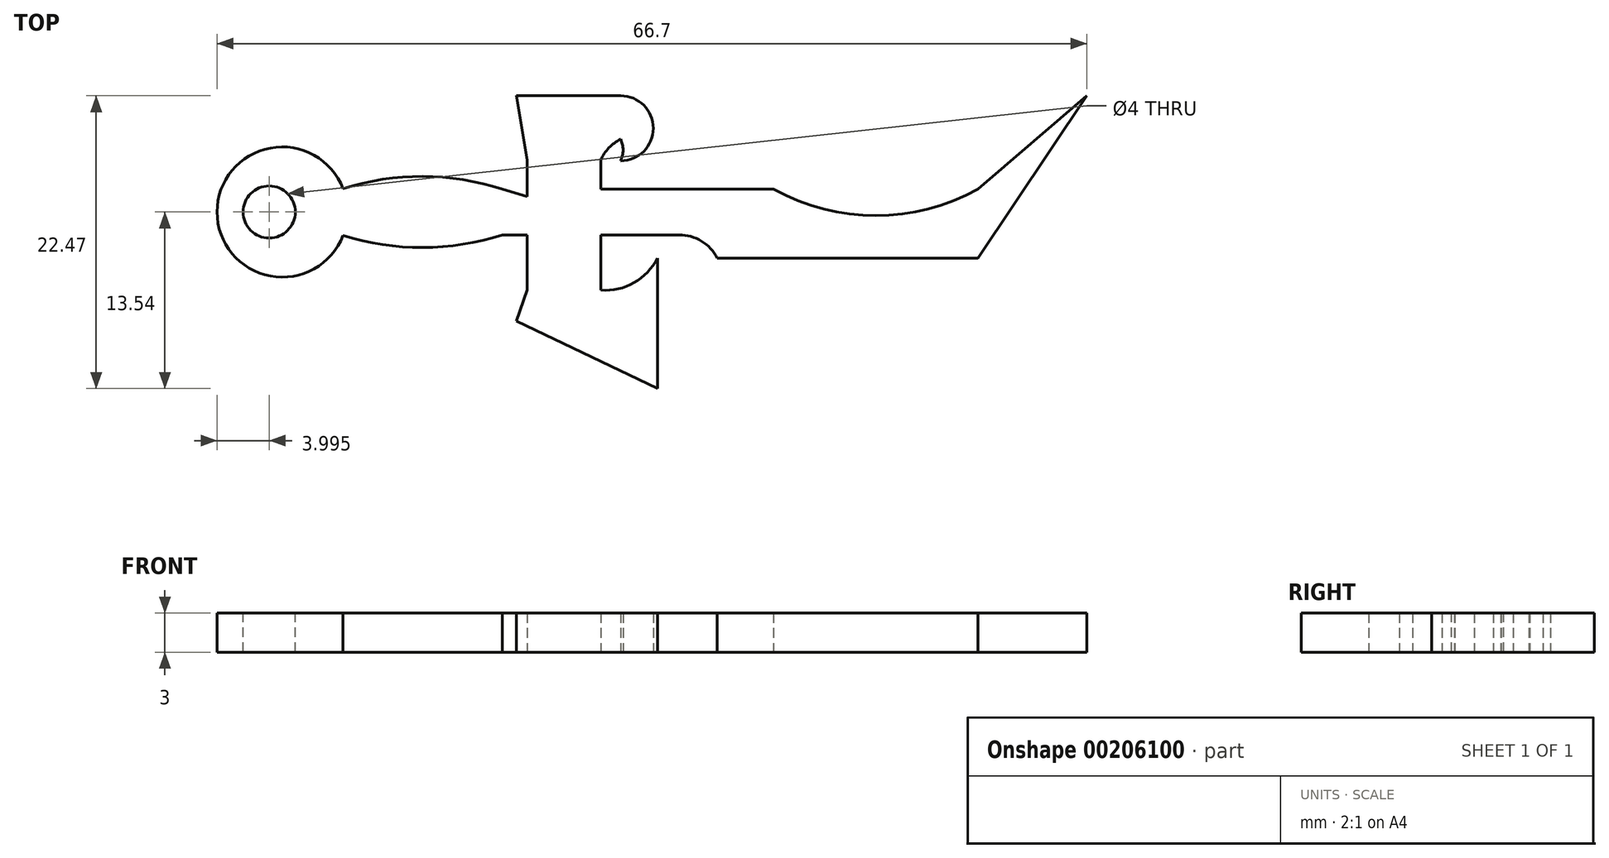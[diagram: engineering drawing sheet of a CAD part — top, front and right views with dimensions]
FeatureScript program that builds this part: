
annotation { "Feature Type Name" : "Feature", "Feature Type Description" : "" }
export const myFeature = defineFeature(function(context is Context, id is Id, definition is map)
    precondition{}
    {
        {
            var Q0;
            Q0=qCreatedBy(makeId("Top.planeOp"),FACE);
            var sketch = newSketch(context, id + "F0", { "sketchPlane" : qUnion([Q0])});
            skArc(sketch, "E0", {"start": v(14.09, 3.5) * mm, "mid": v(7.9, 4.48) * mm, "end": v(1.72, 3.5) * mm});
            skArc(sketch, "E1", {"start": v(1.72, 0) * mm, "mid": v(7.9, -0.98) * mm, "end": v(14.09, 0) * mm});
            skLineSegment(sketch, "E2", {"start": v(14.09, 3.5) * mm, "end": v(14.09, 0) * mm});
            skLineSegment(sketch, "E3", {"start": v(14.09, 3.5) * mm, "end": v(16.01, 2.94) * mm});
            skLineSegment(sketch, "E4", {"start": v(14.09, 0) * mm, "end": v(16.01, 0) * mm});
            skLineSegment(sketch, "E5", {"start": v(16.01, 0) * mm, "end": v(16.01, -4.25) * mm});
            skLineSegment(sketch, "E6", {"start": v(16.01, -4.25) * mm, "end": v(15.17, -6.6) * mm});
            skLineSegment(sketch, "E7", {"start": v(15.17, -6.6) * mm, "end": v(26, -11.8) * mm});
            skLineSegment(sketch, "E8", {"start": v(16.01, 2.94) * mm, "end": v(16.01, 5.75) * mm});
            skLineSegment(sketch, "E9", {"start": v(16.01, 5.75) * mm, "end": v(15.17, 10.68) * mm});
            skLineSegment(sketch, "E10", {"start": v(15.17, 10.68) * mm, "end": v(23.17, 10.68) * mm});
            skArc(sketch, "E11", {"start": v(23.17, 5.68) * mm, "mid": v(25.67, 8.18) * mm, "end": v(23.17, 10.68) * mm});
            skArc(sketch, "E12", {"start": v(23.17, 5.68) * mm, "mid": v(23.35, 6.5) * mm, "end": v(23.17, 7.34) * mm});
            skArc(sketch, "E13", {"start": v(23.17, 7.34) * mm, "mid": v(22.27, 6.68) * mm, "end": v(21.65, 5.75) * mm});
            skLineSegment(sketch, "E14", {"start": v(26, -11.8) * mm, "end": v(26, -1.8) * mm});
            skArc(sketch, "E15", {"start": v(21.65, -4.25) * mm, "mid": v(24.2, -3.68) * mm, "end": v(26, -1.8) * mm});
            skLineSegment(sketch, "E16", {"start": v(21.65, 5.75) * mm, "end": v(21.65, -4.25) * mm});
            skLineSegment(sketch, "E17", {"start": v(21.65, 3.5) * mm, "end": v(34.9, 3.5) * mm});
            skLineSegment(sketch, "E18", {"start": v(21.65, 0) * mm, "end": v(27.65, 0) * mm});
            skArc(sketch, "E19", {"start": v(30.58, -1.8) * mm, "mid": v(29.37, -0.48) * mm, "end": v(27.65, 0) * mm});
            skLineSegment(sketch, "E20", {"start": v(30.58, -1.8) * mm, "end": v(50.58, -1.8) * mm});
            skLineSegment(sketch, "E21", {"start": v(50.58, -1.8) * mm, "end": v(58.92, 10.68) * mm});
            skLineSegment(sketch, "E22", {"start": v(58.92, 10.68) * mm, "end": v(50.58, 3.5) * mm});
            skLineSegment(sketch, "E23", {"start": v(1.72, 3.5) * mm, "end": v(1.72, 1.75) * mm});
            skLineSegment(sketch, "E24", {"start": v(1.72, 1.75) * mm, "end": v(1.72, 0) * mm});
            skLineSegment(sketch, "E25", {"start": v(1.72, 1.75) * mm, "end": v(2.22, 1.75) * mm});
            skCircle(sketch, "E26", {"center": v(-2.78, 1.75) * mm, "radius": 5 * mm});
            skPoint(sketch, "E26.centerSnap0", {"position": v(1.97, 1.75) * mm});
            skArc(sketch, "E27", {"start": v(34.9, 3.5) * mm, "mid": v(42.74, 1.48) * mm, "end": v(50.58, 3.5) * mm});
            skSolve(sketch);
        }
        {
            var Q0;
            Q0=makeQuery(id+"F0.imprint","IMPRINT",FACE,{"disambiguationData":[TD([[makeQuery(id+"F0.imprint","IMPRINT",EDGE,{"derivedFrom":sQuery(id+"F0.wireOp",EDGE,"HvkfksOm-UdQP-Q2aK-ck7c-MZqCCzY5SsJ3")}),1.0]])]});
            var Q1;
            {var subQ4=sQuery(id+"F0.wireOp",EDGE,"E2");Q1=makeQuery(id+"F0.imprint","IMPRINT",FACE,{"disambiguationData":[TD([[makeQuery(id+"F0.imprint","IMPRINT",EDGE,{"derivedFrom":subQ4}),-1.0]])]});}
            var Q2;
            {var subQ1=sQuery(id+"F0.wireOp",EDGE,"E17");Q2=makeQuery(id+"F0.imprint","IMPRINT",FACE,{"disambiguationData":[TD([[makeQuery(id+"F0.imprint","IMPRINT",EDGE,{"derivedFrom":subQ1}),-1.0]])]});}
            var Q3;
            {var subQ0=sQuery(id+"F0.wireOp",EDGE,"jO991LbM-bbrh-6jQi-vaoB-H2DKlpkK7WZ9");var subQ1=makeQuery(id+"F0.imprint","INTERSECT",VERTEX,{"derivedFrom":[subQ0,sQuery(id+"F0.wireOp",EDGE,"OPN9bPB0-msuf-70Mz-ZPV4-m7Wf6nl5FQtI")]});Q3=makeQuery(id+"F0.imprint","IMPRINT",FACE,{"disambiguationData":[TD([[makeQuery(id+"F0.imprint","IMPRINT",EDGE,{"disambiguationData":[TD([[subQ1,-1.0]])],"derivedFrom":subQ0}),1.0]])]});}
            var Q4;
            Q4=makeQuery(id+"F0.imprint","IMPRINT",FACE,{"disambiguationData":[TD([[makeQuery(id+"F0.imprint","IMPRINT",EDGE,{"derivedFrom":sQuery(id+"F0.wireOp",EDGE,"E2")}),1.0]])]});
            var Q5;
            {var subQ4=sQuery(id+"F0.wireOp",EDGE,"E23");Q5=makeQuery(id+"F0.imprint","IMPRINT",FACE,{"disambiguationData":[TD([[makeQuery(id+"F0.imprint","IMPRINT",EDGE,{"derivedFrom":subQ4}),-1.0]])]});}
            var Q6;
            {var subQ0=sQuery(id+"F0.wireOp",EDGE,"E23");Q6=makeQuery(id+"F0.imprint","IMPRINT",FACE,{"disambiguationData":[TD([[makeQuery(id+"F0.imprint","IMPRINT",EDGE,{"derivedFrom":subQ0}),1.0]])]});}
            var Q7;
            {var subQ0=sQuery(id+"F0.wireOp",EDGE,"E24");Q7=makeQuery(id+"F0.imprint","IMPRINT",FACE,{"disambiguationData":[TD([[makeQuery(id+"F0.imprint","IMPRINT",EDGE,{"derivedFrom":subQ0}),1.0]])]});}
            extrude(context, id + "F1", {"entities" : qUnion([Q0, Q1, Q2, Q3, Q4, Q5, Q6, Q7]), "depth" : 3 * mm, "offsetDistance" : 25 * mm});
        }
        {
            var Q0;
            Q0=makeQuery(id+"F1.opExtrude","CAP_FACE",FACE,{"disambiguationData":[OSD([sQuery(id+"F0.wireOp",EDGE,"E0"),sQuery(id+"F0.wireOp",EDGE,"E1"),sQuery(id+"F0.wireOp",EDGE,"E3"),sQuery(id+"F0.wireOp",EDGE,"E4"),sQuery(id+"F0.wireOp",EDGE,"E5"),sQuery(id+"F0.wireOp",EDGE,"E6"),sQuery(id+"F0.wireOp",EDGE,"E7"),sQuery(id+"F0.wireOp",EDGE,"E8"),sQuery(id+"F0.wireOp",EDGE,"E9"),sQuery(id+"F0.wireOp",EDGE,"E10"),sQuery(id+"F0.wireOp",EDGE,"E11"),sQuery(id+"F0.wireOp",EDGE,"E12"),sQuery(id+"F0.wireOp",EDGE,"E13"),sQuery(id+"F0.wireOp",EDGE,"E14"),sQuery(id+"F0.wireOp",EDGE,"E15"),sQuery(id+"F0.wireOp",EDGE,"E16"),sQuery(id+"F0.wireOp",EDGE,"E17"),sQuery(id+"F0.wireOp",EDGE,"E18"),sQuery(id+"F0.wireOp",EDGE,"E19"),sQuery(id+"F0.wireOp",EDGE,"E20"),sQuery(id+"F0.wireOp",EDGE,"E21"),sQuery(id+"F0.wireOp",EDGE,"E22"),sQuery(id+"F0.wireOp",EDGE,"E26"),sQuery(id+"F0.wireOp",EDGE,"jO991LbM-bbrh-6jQi-vaoB-H2DKlpkK7WZ9"),sQuery(id+"F0.wireOp",EDGE,"OPN9bPB0-msuf-70Mz-ZPV4-m7Wf6nl5FQtI"),sQuery(id+"F0.wireOp",EDGE,"CZV3FKTg-91Ai-dbvC-hyIH-rp91pPgkU6oQ")])],"isStart":false});
            var sketch = newSketch(context, id + "F2", { "sketchPlane" : qUnion([Q0])});
            skCircle(sketch, "E28", {"center": v(-3.78, 1.75) * mm, "radius": 2 * mm});
            skSolve(sketch);
        }
        {
            var Q0;
            Q0=sQuery(id+"F2.wireOp",VERTEX,"E28.center");
            var Q1;
            Q1=makeQuery(id+"F1.opExtrude","SWEPT_BODY",BODY,{"disambiguationData":[OSD([sQuery(id+"F0.wireOp",EDGE,"E0"),sQuery(id+"F0.wireOp",EDGE,"E1"),sQuery(id+"F0.wireOp",EDGE,"E3"),sQuery(id+"F0.wireOp",EDGE,"E4"),sQuery(id+"F0.wireOp",EDGE,"E5"),sQuery(id+"F0.wireOp",EDGE,"E6"),sQuery(id+"F0.wireOp",EDGE,"E7"),sQuery(id+"F0.wireOp",EDGE,"E8"),sQuery(id+"F0.wireOp",EDGE,"E9"),sQuery(id+"F0.wireOp",EDGE,"E10"),sQuery(id+"F0.wireOp",EDGE,"E11"),sQuery(id+"F0.wireOp",EDGE,"E12"),sQuery(id+"F0.wireOp",EDGE,"E13"),sQuery(id+"F0.wireOp",EDGE,"E14"),sQuery(id+"F0.wireOp",EDGE,"E15"),sQuery(id+"F0.wireOp",EDGE,"E16"),sQuery(id+"F0.wireOp",EDGE,"E17"),sQuery(id+"F0.wireOp",EDGE,"E18"),sQuery(id+"F0.wireOp",EDGE,"E19"),sQuery(id+"F0.wireOp",EDGE,"E20"),sQuery(id+"F0.wireOp",EDGE,"E21"),sQuery(id+"F0.wireOp",EDGE,"E22"),sQuery(id+"F0.wireOp",EDGE,"E26"),sQuery(id+"F0.wireOp",EDGE,"jO991LbM-bbrh-6jQi-vaoB-H2DKlpkK7WZ9"),sQuery(id+"F0.wireOp",EDGE,"OPN9bPB0-msuf-70Mz-ZPV4-m7Wf6nl5FQtI"),sQuery(id+"F0.wireOp",EDGE,"CZV3FKTg-91Ai-dbvC-hyIH-rp91pPgkU6oQ")])]});
            hole(context, id + "F3", {"style" : HoleStyle.SIMPLE, "endStyle" : HoleEndStyle.THROUGH, "holeDiameter" : 4 * mm, "locations" : qUnion([Q0]), "scope" : qUnion([Q1]), "isTappedThrough" : true});
        }
    });
